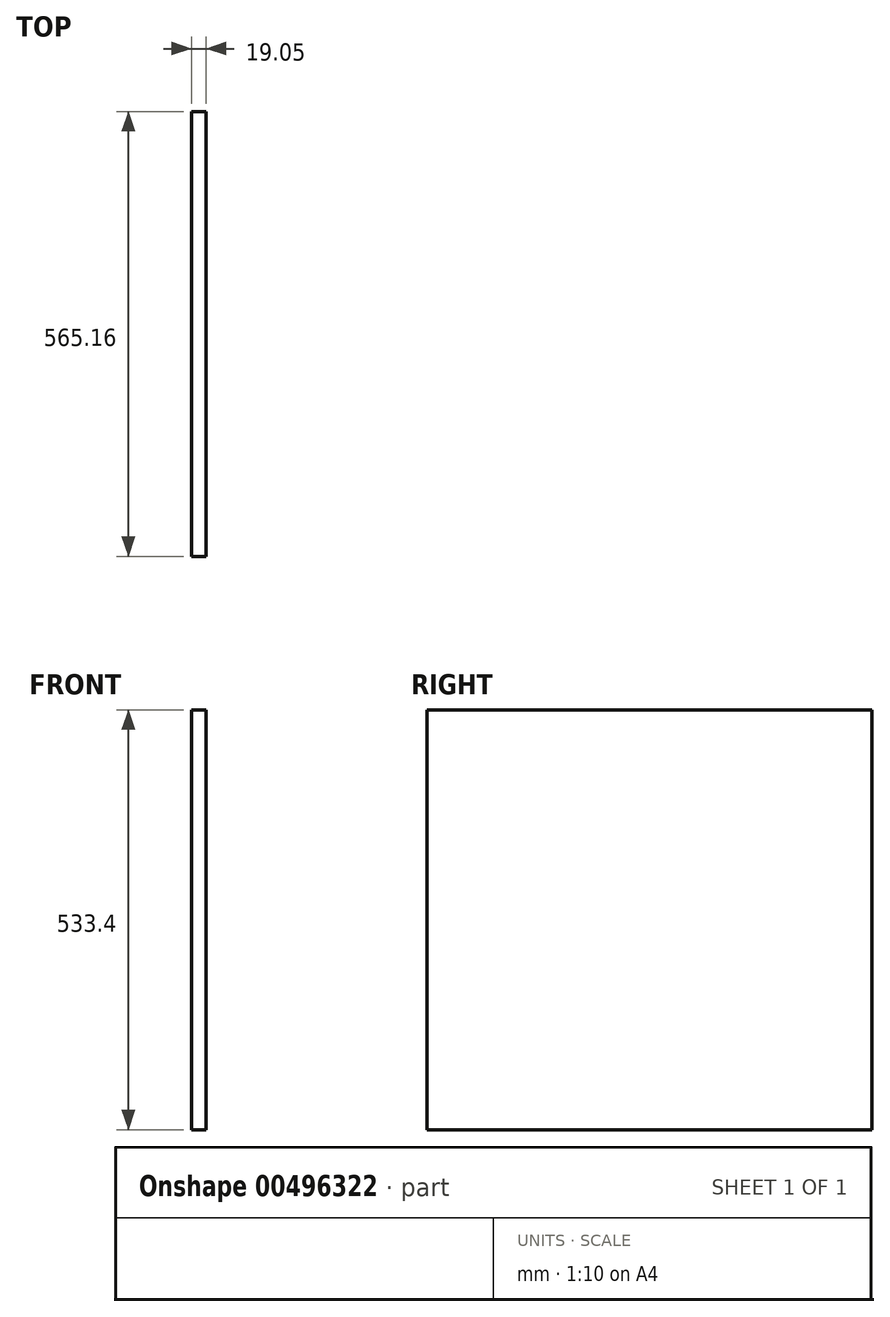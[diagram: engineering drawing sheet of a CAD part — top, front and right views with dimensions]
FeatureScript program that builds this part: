
annotation { "Feature Type Name" : "Feature", "Feature Type Description" : "" }
export const myFeature = defineFeature(function(context is Context, id is Id, definition is map)
    precondition{}
    {
        {
            var Q0;
            Q0=qCreatedBy(makeId("Right.planeOp"),FACE);
            var sketch = newSketch(context, id + "F0", { "sketchPlane" : qUnion([Q0])});
            skLineSegment(sketch, "E0.bottom", {"start": v(282.58, -266.7) * mm, "end": v(-282.58, -266.7) * mm});
            skLineSegment(sketch, "E0.top", {"start": v(282.58, 266.7) * mm, "end": v(-282.58, 266.7) * mm});
            skLineSegment(sketch, "E0.left", {"start": v(282.58, -266.7) * mm, "end": v(282.58, 266.7) * mm});
            skLineSegment(sketch, "E0.right", {"start": v(-282.58, -266.7) * mm, "end": v(-282.58, 266.7) * mm});
            skPoint(sketch, "E0.middle", {"position": v(0, 0) * mm});
            skSolve(sketch);
        }
        {
            var Q0;
            Q0=qSketchRegion(id+"F0",true);
            extrude(context, id + "F1", {"entities" : qUnion([Q0]), "depth" : 19.05 * mm});
        }
    });
